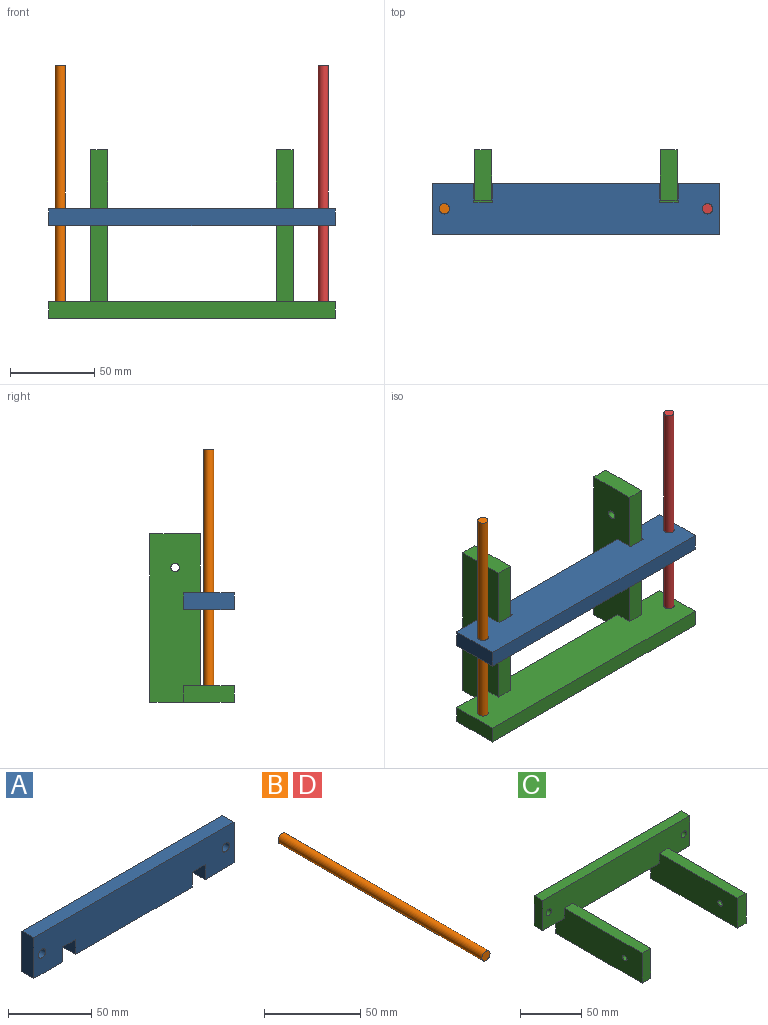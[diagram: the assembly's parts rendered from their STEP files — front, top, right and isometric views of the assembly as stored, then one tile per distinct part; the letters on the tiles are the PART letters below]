
ASSEMBLY  parts=4 mates=3
PART A: 16 faces, bbox 170.1x10x30 mm
  f0: plane 30x10mm, normal (-1,0,0), area 300mm2, adj f1,f12,f14,f15
  f1: plane 24.5x10mm, normal (0,0,-1), area 245mm2, adj f0,f2,f14,f15
  f2: plane 11x10mm, normal (1,0,0), area 110mm2, adj f1,f3,f14,f15
  f3: plane 11x10mm, normal (0,0,-1), area 110mm2, adj f2,f4,f14,f15
  f4: plane 11x10mm, normal (-1,0,0), area 110mm2, adj f3,f5,f14,f15
  f5: plane 99.12x10mm, normal (0,0,-1), area 991.2mm2, adj f4,f6,f14,f15
  f6: plane 11x10mm, normal (1,0,0), area 110mm2, adj f5,f7,f14,f15
  f7: plane 11x10mm, normal (0,0,-1), area 110mm2, adj f6,f8,f14,f15
  f8: plane 11x10mm, normal (-1,0,0), area 110mm2, adj f7,f9,f14,f15
  f9: plane 24.5x10mm, normal (0,0,-1), area 245mm2, adj f8,f10,f14,f15
  f10: plane 30x10mm, normal (1,0,0), area 300mm2, adj f9,f12,f14,f15
  f11: cylinder r=3.1mm len=10mm, axis (0,1,0), area 194.8mm2, adj f14,f15
  f12: plane 170.12x10mm, normal (0,0,1), area 1701.2mm2, adj f0,f10,f14,f15
  f13: cylinder r=3.1mm len=10mm, axis (0,1,0), area 194.8mm2, adj f14,f15
  f14: plane 170.12x30mm, normal (0,-1,0), area 4801.3mm2, adj f0,f1,f2,f3,f4,f5,f6,f7
  f15: plane 170.12x30mm, normal (0,1,0), area 4801.3mm2, adj f0,f1,f2,f3,f4,f5,f6,f7
PART B: 3 faces, bbox 6x150x6 mm
  f0: cylinder r=3mm len=150mm, axis (0,1,0), area 2827.4mm2, adj f1,f2
  f1: plane 6x6mm, normal (0,-1,0), area 28.3mm2, adj f0
  f2: plane 6x6mm, normal (0,1,0), area 28.3mm2, adj f0
PART C: 22 faces, bbox 170x100x50 mm
  f0: plane 170x30mm, normal (0,-1,0), area 4841.6mm2, adj f1,f2,f3,f5,f6,f7,f8,f9
  f1: plane 100x30mm, normal (1,0,0), area 2880.4mm2, adj f0,f2,f13,f15,f16,f17,f20
  f2: plane 100x10mm, normal (0,0,-1), area 1000mm2, adj f0,f1,f3,f15
  f3: plane 100x30mm, normal (-1,0,0), area 2880.4mm2, adj f0,f2,f4,f15,f18,f19,f21
  f4: plane 100x10mm, normal (0,0,-1), area 1000mm2, adj f3,f5,f15,f19
  f5: plane 100x30mm, normal (1,0,0), area 2880.4mm2, adj f0,f4,f6,f15,f18,f19,f21
  f6: plane 25x10mm, normal (0,0,-1), area 250mm2, adj f0,f5,f7,f15
  f7: plane 30x10mm, normal (1,0,0), area 300mm2, adj f0,f6,f8,f15
  f8: plane 170x10mm, normal (0,0,1), area 1700mm2, adj f0,f7,f9,f15
  f9: plane 30x10mm, normal (-1,0,0), area 300mm2, adj f0,f8,f10,f15
  f10: plane 25x10mm, normal (0,0,-1), area 250mm2, adj f0,f9,f11,f15
  f11: plane 100x30mm, normal (-1,0,0), area 2880.4mm2, adj f0,f10,f13,f15,f16,f17,f20
  f12: cylinder r=3.05mm len=10mm, axis (0,1,0), area 191.6mm2, adj f0,f15
  f13: plane 100x10mm, normal (0,0,-1), area 1000mm2, adj f1,f11,f15,f17
  f14: cylinder r=3.05mm len=10mm, axis (0,1,0), area 191.6mm2, adj f0,f15
  f15: plane 170x50mm, normal (0,1,0), area 5441.6mm2, adj f1,f2,f3,f4,f5,f6,f7,f8
  f16: plane 90x10mm, normal (0,0,1), area 900mm2, adj f0,f1,f11,f17
  f17: plane 30x10mm, normal (0,-1,0), area 300mm2, adj f1,f11,f13,f16
  f18: plane 90x10mm, normal (0,0,1), area 900mm2, adj f0,f3,f5,f19
  f19: plane 30x10mm, normal (0,-1,0), area 300mm2, adj f3,f4,f5,f18
  f20: cylinder r=2.5mm len=10mm, axis (-1,0,0), area 157.1mm2, adj f1,f11
  f21: cylinder r=2.5mm len=10mm, axis (-1,0,0), area 157.1mm2, adj f3,f5
PART D: same geometry as B
PLACE A rot(axis=(1,0,0),90deg) t=(113.96,49.75,115.89)mm
PLACE B rot(axis=(1,0,0),90deg) t=(35.9,49.75,200.89)mm
PLACE C rot(axis=(0,0.71,-0.71),180deg) t=(113.9,49.75,50.89)mm fixed
PLACE D rot(axis=(1,0,0),90deg) t=(191.9,49.75,200.89)mm
MATE fastened D.f0 <-> C.f12  axis (0,0,-1) through (191.9,49.75,50.89)mm
MATE fastened B.f0 <-> C.f14  axis (0,0,-1) through (35.9,49.75,50.89)mm
MATE slider A.f11 <-> B.f0  axis (0,0,-1) through (35.9,49.75,105.89)mm
